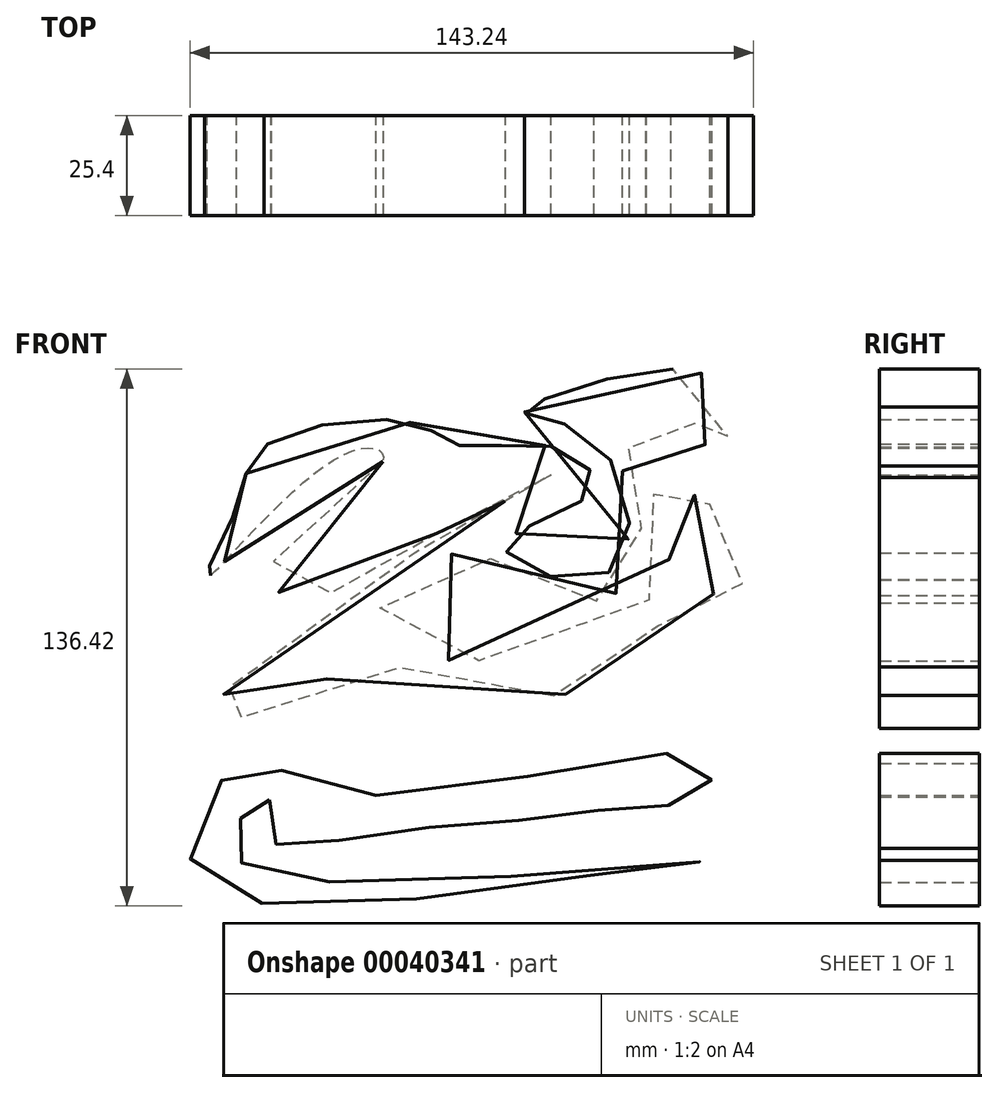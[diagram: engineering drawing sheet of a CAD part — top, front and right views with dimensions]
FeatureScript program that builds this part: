
annotation { "Feature Type Name" : "Feature", "Feature Type Description" : "" }
export const myFeature = defineFeature(function(context is Context, id is Id, definition is map)
    precondition{}
    {
        {
            var Q0;
            Q0=qCreatedBy(makeId("Front.planeOp"),FACE);
            var sketch = newSketch(context, id + "F0", { "sketchPlane" : qUnion([Q0])});
            skFitSpline(sketch, "E0", {"points": [v(-19.74, 43.31) * mm, v(-49.93, 13.82) * mm, v(-34.6, 9.64) * mm, v(-12.08, 21.48) * mm, v(23, 39.83) * mm, v(-50.4, -6.15) * mm, v(-63.4, -24.5) * mm, v(-22.3, -9.17) * mm, v(29.03, -15.44) * mm, v(56.44, 6.62) * mm, v(71.77, 12.43) * mm, v(72, 24.97) * mm, v(47.38, 39.13) * mm, v(52.49, 28.22) * mm, v(37.4, 0) * mm, v(-21.13, 0) * mm, v(0, 20.09) * mm, v(27.87, 7.55) * mm, v(46.91, 18) * mm, v(42.27, 34.72) * mm, v(43.66, 48.42) * mm, v(56.9, 56.55) * mm, v(65.03, 42.15) * mm, v(67.35, 58.88) * mm, v(49.7, 66.54) * mm, v(16.26, 56.09) * mm, v(33.9, 48.66) * mm, v(37.4, 14.98) * mm, v(11.38, 21.72) * mm, v(33.21, 35.65) * mm, v(24.39, 46.8) * mm, v(0, 47.26) * mm, v(-12.08, 53.07) * mm, v(-49.7, 47.26) * mm, v(-57.13, 31.24) * mm, v(-64.8, 13.35) * mm, v(-29.03, 45.4) * mm, v(-19.74, 43.31) * mm]});
            skSolve(sketch);
        }
        {
            var Q0;
            Q0=makeQuery(id+"F0.imprint","IMPRINT",FACE,{"disambiguationData":[TD([[makeQuery(id+"F0.imprint","IMPRINT",EDGE,{"derivedFrom":sQuery(id+"F0.wireOp",EDGE,"E0")}),1.0]])]});
            extrude(context, id + "F1", {"entities" : qUnion([Q0]), "depth" : 25.4 * mm});
        }
        {
            var Q0;
            Q0=qCreatedBy(makeId("Front.planeOp"),FACE);
            var sketch = newSketch(context, id + "F2", { "sketchPlane" : qUnion([Q0])});
            skFitSpline(sketch, "E1", {"points": [v(-48.54, -42.62) * mm, v(-47.38, -53.3) * mm, v(-26.94, -52.14) * mm, v(14.17, -47.96) * mm, v(44.36, -44.48) * mm, v(61.78, -41) * mm, v(61.78, -32.17) * mm, v(-25.78, -41.22) * mm, v(-56.2, -34.26) * mm, v(-67.35, -61.43) * mm, v(31.12, -62.13) * mm, v(62.48, -58.18) * mm, v(-48.54, -62.13) * mm, v(-56.9, -54.23) * mm, v(-53.65, -43.78) * mm, v(-48.54, -42.62) * mm]});
            skSolve(sketch);
        }
        {
            var Q0;
            Q0=makeQuery(id+"F2.imprint","IMPRINT",FACE,{"disambiguationData":[TD([[makeQuery(id+"F2.imprint","IMPRINT",EDGE,{"derivedFrom":sQuery(id+"F2.wireOp",EDGE,"E1")}),1.0]])]});
            extrude(context, id + "F3", {"entities" : qUnion([Q0]), "depth" : 25.4 * mm});
        }
    });
